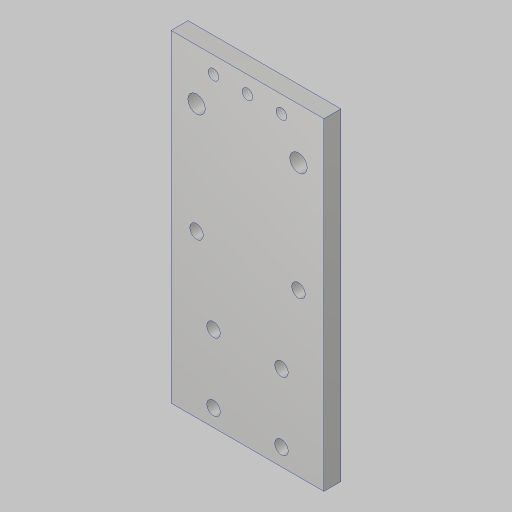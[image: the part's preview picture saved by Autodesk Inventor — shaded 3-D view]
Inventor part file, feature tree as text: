
AUTODESK INVENTOR PART (.ipt)
format: ipt  version: 2023.5 (Build 275446000, 446)  size: 267,264 bytes
history: native  units: in
note: dims shown in document units (in); Inventor stores cm internally (conversion verified against a paired STEP export)
features: hole x3, sketch x2, extrude x1
ambient origin geometry x8: Origin, YZ Plane, XZ Plane, XY Plane, X Axis, Y Axis, Z Axis, Center Point
bodies: Solid1 (feature_tree)
feature tree (6):
  sketch  "Sketch1"  dims[d0=0.257in d1=1.5in]
  extrude  "Extrusion1"  Depth=1.5in
  hole  "Hole1"  [1 undecoded]
  hole  "Hole2"  [1 undecoded]
  hole  "Hole3"  [1 undecoded]
  sketch  "Sketch2"  dims[d4=4.0in d6=0.25in d7=0.0in d8=1.5in d9=2.375in d10=0.201in d11=0.75in d12=0.385in d13=0.25in d14=0.5635in d15=1.0in d16=0.8108in d17=6.0in d18=2.25in d19=0.25in d20=4.75in d21=1.0in d22=0.156in d23=0.38in d24=0.385in d25=0.25in d26=0.5635in d27=1.0in d28=0.8108in d29=0.25in d32=1.0in d33=1.0in d34=0.25in d35=0.201in d36=0.38in d37=0.385in d38=0.25in d39=0.5635in d40=1.0in d41=0.8108in]
note: 3 required parameter values undecoded (feature->parameter linkage not recoverable at this tier; creation-order binding heuristic only, values carry confidence <= 0.55)
